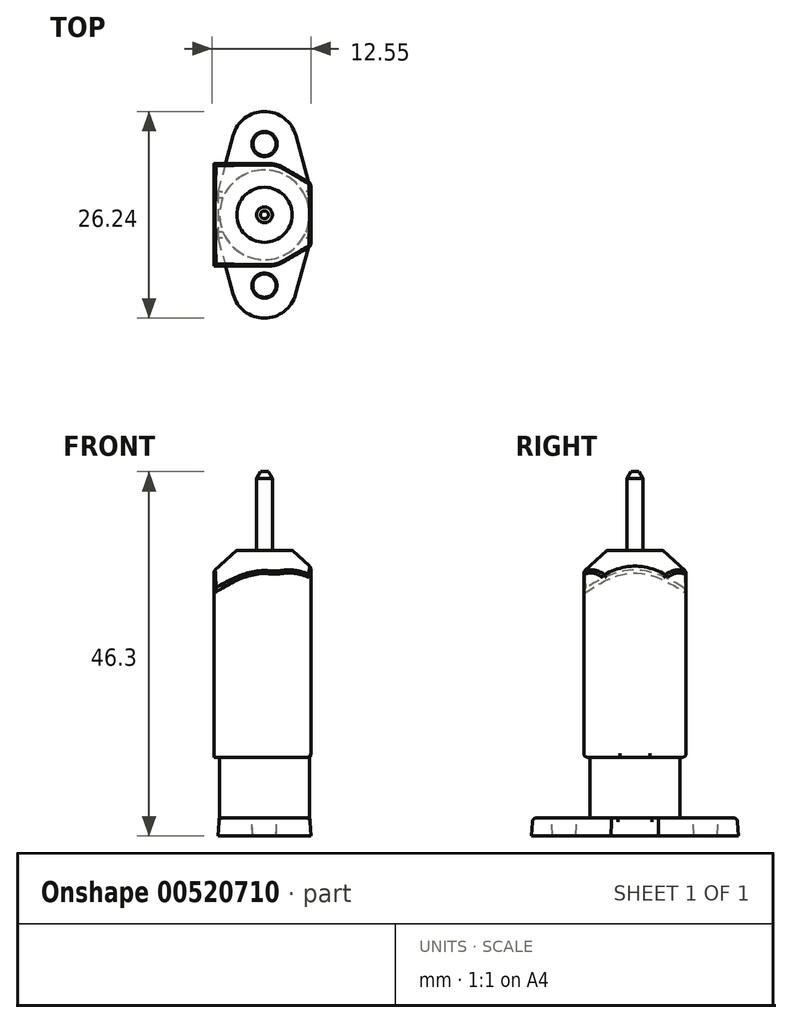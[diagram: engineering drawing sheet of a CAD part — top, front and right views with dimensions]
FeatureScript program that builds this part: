
annotation { "Feature Type Name" : "Feature", "Feature Type Description" : "" }
export const myFeature = defineFeature(function(context is Context, id is Id, definition is map)
    precondition{}
    {
        {
            var Q0;
            Q0=qCreatedBy(makeId("Top.planeOp"),FACE);
            var sketch = newSketch(context, id + "F0", { "sketchPlane" : qUnion([Q0])});
            skLineSegment(sketch, "E0", {"start": v(-5.77, 3) * mm, "end": v(-5.77, -3) * mm});
            skLineSegment(sketch, "E1", {"start": v(-5.77, -3) * mm, "end": v(-3.87, -10.04) * mm});
            skLineSegment(sketch, "E2", {"start": v(-5.77, 3) * mm, "end": v(-3.86, 10.05) * mm});
            skLineSegment(sketch, "E3", {"start": v(3.86, 10.04) * mm, "end": v(5.76, 3) * mm});
            skLineSegment(sketch, "E4", {"start": v(5.76, 3) * mm, "end": v(5.76, -3) * mm});
            skLineSegment(sketch, "E5", {"start": v(5.76, -3) * mm, "end": v(3.85, -10.05) * mm});
            skArc(sketch, "E6", {"start": v(3.86, 10.04) * mm, "mid": v(0, 13) * mm, "end": v(-3.86, 10.05) * mm});
            skArc(sketch, "E7", {"start": v(-3.87, -10.04) * mm, "mid": v(-0.01, -13) * mm, "end": v(3.85, -10.05) * mm});
            skCircle(sketch, "E8", {"center": v(0, 9) * mm, "radius": 1.6 * mm});
            skCircle(sketch, "E9", {"center": v(0, -9) * mm, "radius": 1.6 * mm});
            skLineSegment(sketch, "E10", {"start": v(0, 9) * mm, "end": v(0, 0) * mm, "construction": true});
            skLineSegment(sketch, "E11", {"start": v(0, 0) * mm, "end": v(0, -9) * mm, "construction": true});
            skCircle(sketch, "E12", {"center": v(0, 0) * mm, "radius": 5.7 * mm});
            skCircle(sketch, "E13", {"center": v(0, 0) * mm, "radius": 1 * mm});
            skSolve(sketch);
        }
        {
            var Q0;
            Q0=makeQuery(id+"F0.imprint","IMPRINT",FACE,{"disambiguationData":[TD([[makeQuery(id+"F0.imprint","IMPRINT",EDGE,{"derivedFrom":sQuery(id+"F0.wireOp",EDGE,"E0")}),1.0]])]});
            var Q1;
            Q1=makeQuery(id+"F0.imprint","IMPRINT",FACE,{"disambiguationData":[TD([[makeQuery(id+"F0.imprint","IMPRINT",EDGE,{"derivedFrom":sQuery(id+"F0.wireOp",EDGE,"E12")}),1.0]])]});
            var Q2;
            Q2=makeQuery(id+"F0.imprint","IMPRINT",FACE,{"disambiguationData":[TD([[makeQuery(id+"F0.imprint","IMPRINT",EDGE,{"derivedFrom":sQuery(id+"F0.wireOp",EDGE,"E13")}),1.0]])]});
            extrude(context, id + "F1", {"entities" : qUnion([Q0, Q1, Q2]), "oppositeDirection" : true, "depth" : 2.3 * mm, "offsetDistance" : 25 * mm, "hasDraft" : true, "draftAngle" : 3 * degree});
        }
        {
            var Q0;
            Q0=makeQuery(id+"F0.imprint","IMPRINT",FACE,{"disambiguationData":[TD([[makeQuery(id+"F0.imprint","IMPRINT",EDGE,{"derivedFrom":sQuery(id+"F0.wireOp",EDGE,"E12")}),1.0]])]});
            extrude(context, id + "F2", {"entities" : qUnion([Q0]), "operationType" : NewBodyOperationType.ADD, "depth" : 7.7 * mm, "offsetDistance" : 25 * mm});
        }
        {
            var Q0;
            Q0=makeQuery(id+"F2.opExtrude","CAP_FACE",FACE,{"disambiguationData":[OSD([sQuery(id+"F0.wireOp",EDGE,"E12")])],"isStart":false});
            var sketch = newSketch(context, id + "F3", { "sketchPlane" : qUnion([Q0])});
            skLineSegment(sketch, "E14", {"start": v(5.88, 4) * mm, "end": v(5.88, -4) * mm});
            skLineSegment(sketch, "E15", {"start": v(-6.42, 6.5) * mm, "end": v(-6.42, -6.5) * mm});
            skLineSegment(sketch, "E16", {"start": v(-6.42, 6.5) * mm, "end": v(0.58, 6.5) * mm});
            skLineSegment(sketch, "E17", {"start": v(-6.42, -6.5) * mm, "end": v(0.58, -6.5) * mm});
            skLineSegment(sketch, "E18", {"start": v(5.88, 4) * mm, "end": v(2.4, 6.02) * mm});
            skLineSegment(sketch, "E19", {"start": v(5.88, -4) * mm, "end": v(2.4, -6.02) * mm});
            skArc(sketch, "E20", {"start": v(2.4, 6.02) * mm, "mid": v(1.52, 6.38) * mm, "end": v(0.58, 6.5) * mm});
            skArc(sketch, "E21", {"start": v(0.58, -6.5) * mm, "mid": v(1.52, -6.38) * mm, "end": v(2.4, -6.02) * mm});
            skSolve(sketch);
        }
        {
            var Q0;
            Q0 = qSketchRegion(id + "F3", true);
            extrude(context, id + "F4", {"entities" : qUnion([Q0]), "operationType" : NewBodyOperationType.ADD, "depth" : 26.3 * mm, "offsetDistance" : 25 * mm});
        }
        {
            var Q0;
            Q0=makeQuery(id+"F0.imprint","IMPRINT",FACE,{"disambiguationData":[TD([[makeQuery(id+"F0.imprint","IMPRINT",EDGE,{"derivedFrom":sQuery(id+"F0.wireOp",EDGE,"E13")}),1.0]])]});
            extrude(context, id + "F5", {"entities" : qUnion([Q0]), "operationType" : NewBodyOperationType.ADD, "depth" : 44 * mm, "offsetDistance" : 25 * mm});
        }
        {
            var Q0;
            Q0=makeQuery(id+"F5.opExtrude","CAP_EDGE",EDGE,{"disambiguationData":[OSD([sQuery(id+"F0.wireOp",EDGE,"E13")])],"isStart":false});
            chamfer(context, id + "F6", {"entities" : qUnion([Q0]), "chamferType" : ChamferType.OFFSET_ANGLE, "width" : 0.5 * mm, "oppositeDirection" : false, "angle" : 60 * degree, "tangentPropagation" : true});
        }
        {
            var Q0;
            Q0=makeQuery(id+"F4.opExtrude","CAP_FACE",FACE,{"disambiguationData":[OSD([sQuery(id+"F3.wireOp",EDGE,"E14"),sQuery(id+"F3.wireOp",EDGE,"E15"),sQuery(id+"F3.wireOp",EDGE,"E16"),sQuery(id+"F3.wireOp",EDGE,"E17"),sQuery(id+"F3.wireOp",EDGE,"E18"),sQuery(id+"F3.wireOp",EDGE,"E19"),sQuery(id+"F3.wireOp",EDGE,"E20"),sQuery(id+"F3.wireOp",EDGE,"E21")])],"isStart":false});
            var sketch = newSketch(context, id + "F7", { "sketchPlane" : qUnion([Q0])});
            skCircle(sketch, "E22", {"center": v(0, 0) * mm, "radius": 3.5 * mm});
            skCircle(sketch, "E23", {"center": v(0, 0) * mm, "radius": 9.14 * mm});
            skSolve(sketch);
        }
        {
            var Q0;
            Q0=makeQuery(id+"F7.imprint","IMPRINT",FACE,{"disambiguationData":[TD([[makeQuery(id+"F7.imprint","IMPRINT",EDGE,{"derivedFrom":makeQuery(id+"F4.opExtrude","CAP_EDGE",EDGE,{"disambiguationData":[OSD([sQuery(id+"F3.wireOp",EDGE,"E14")])],"isStart":false})}),1.0]])]});
            var Q1;
            {var subQ1=makeQuery(id+"F4.opExtrude","CAP_EDGE",EDGE,{"disambiguationData":[OSD([sQuery(id+"F3.wireOp",EDGE,"E15")])],"isStart":false});Q1=makeQuery(id+"F7.imprint","IMPRINT",FACE,{"disambiguationData":[TD([[makeQuery(id+"F7.imprint","IMPRINT",EDGE,{"derivedFrom":subQ1}),-1.0]])]});}
            var Q2;
            Q2=makeQuery(id+"F7.imprint","IMPRINT",FACE,{"disambiguationData":[TD([[makeQuery(id+"F7.imprint","IMPRINT",EDGE,{"derivedFrom":sQuery(id+"F7.wireOp",EDGE,"E22")}),-1.0]])]});
            extrude(context, id + "F8", {"entities" : qUnion([Q0, Q1, Q2]), "oppositeDirection" : true, "depth" : 5 * mm, "offsetDistance" : 25 * mm});
        }
        {
            var Q0;
            Q0=makeQuery(id+"F8.opExtrude","CAP_EDGE",EDGE,{"disambiguationData":[OSD([sQuery(id+"F7.wireOp",EDGE,"E22")])],"isStart":false});
            chamfer(context, id + "F9", {"entities" : qUnion([Q0]), "chamferType" : ChamferType.OFFSET_ANGLE, "width" : 5.5 * mm, "oppositeDirection" : false, "angle" : 42.25 * degree, "tangentPropagation" : true});
        }
        {
            var Q0;
            Q0=makeQuery(id+"F8.opExtrude","SWEPT_BODY",BODY,{"disambiguationData":[OSD([sQuery(id+"F7.wireOp",EDGE,"E22"),sQuery(id+"F7.wireOp",EDGE,"E23")])]});
            var Q1;
            Q1=makeQuery(id+"F1.opExtrude","SWEPT_BODY",BODY,{"disambiguationData":[OSD([sQuery(id+"F0.wireOp",EDGE,"E0"),sQuery(id+"F0.wireOp",EDGE,"E1"),sQuery(id+"F0.wireOp",EDGE,"E2"),sQuery(id+"F0.wireOp",EDGE,"E3"),sQuery(id+"F0.wireOp",EDGE,"E4"),sQuery(id+"F0.wireOp",EDGE,"E5"),sQuery(id+"F0.wireOp",EDGE,"E6"),sQuery(id+"F0.wireOp",EDGE,"E7"),sQuery(id+"F0.wireOp",EDGE,"E8"),sQuery(id+"F0.wireOp",EDGE,"E9")])]});
            booleanBodies(context, id + "F10", {"operationType" : BooleanOperationType.SUBTRACTION, "tools" : qUnion([Q0]), "targets" : qUnion([Q1])});
        }
        {
            var Q0;
            Q0=makeQuery(id+"F10.opBoolean","COPY",FACE,{"derivedFrom":makeQuery(id+"F9.opChamfer","BLEND_FACE",FACE,{"disambiguationData":[OSD([sQuery(id+"F7.wireOp",EDGE,"E22")])]})});
            var Q1;
            Q1=makeQuery(id+"F4.opExtrude","SWEPT_FACE",FACE,{"disambiguationData":[OSD([sQuery(id+"F3.wireOp",EDGE,"E21")])]});
            var Q2;
            Q2=makeQuery(id+"F4.opExtrude","SWEPT_FACE",FACE,{"disambiguationData":[OSD([sQuery(id+"F3.wireOp",EDGE,"E14")])]});
            var Q3;
            Q3=makeQuery(id+"F4.opExtrude","SWEPT_FACE",FACE,{"disambiguationData":[OSD([sQuery(id+"F3.wireOp",EDGE,"E20")])]});
            var Q4;
            Q4=makeQuery(id+"F1.opExtrude","CAP_EDGE",EDGE,{"disambiguationData":[OSD([sQuery(id+"F0.wireOp",EDGE,"E7")])],"isStart":true});
            var Q5;
            Q5=makeQuery(id+"F1.opExtrude","CAP_EDGE",EDGE,{"disambiguationData":[OSD([sQuery(id+"F0.wireOp",EDGE,"E6")])],"isStart":true});
            var Q6;
            Q6=makeQuery(id+"F1.opExtrude","CAP_EDGE",EDGE,{"disambiguationData":[OSD([sQuery(id+"F0.wireOp",EDGE,"E0")])],"isStart":true});
            var Q7;
            Q7=makeQuery(id+"F1.opExtrude","CAP_EDGE",EDGE,{"disambiguationData":[OSD([sQuery(id+"F0.wireOp",EDGE,"E4")])],"isStart":true});
            fillet(context, id + "F11", {"entities" : qUnion([Q0, Q1, Q2, Q3, Q4, Q5, Q6, Q7]), "radius" : 0.5 * mm, "tangentPropagation" : true, "allowEdgeOverflow" : false});
        }
    });
